# Revit family: Sink-Under_Mount-Lavatory-KOHLER-Bachata-K-2609_1
name_source: partatom
category: Plumbing Fixtures
units: mm (PartAtom-declared; Revit-internal decimal feet)

## family parameters
Cut with Voids When Loaded = No
Host = Face
OmniClass Number = 23.45.05.14.14
OmniClass Title = Sinks/Lavatories
Part Type = Normal
Room Calculation Point = No
Round Connector Dimension = Use Diameter
Shared = No

## types (4) — shared parameters
ADA Compliant = Yes
Assembly Code = D2010400
CW Connection = No
Cold Water Inlet = Cold Water Inlet
Date Modified = 11/24/2024
Default Elevation = 34"
Description = 20 Inch Oval Drop-In/Undermount Bathroom Sink
Drain Included = No
HW Connection = No
Height = 7 3/8"
Hot Water Inlet = Hot Water Inlet
Length = 19 7/8"
Manufacturer = Kohler Co.
MasterFormat 2014 = 22 41 16
MasterFormat 2014 Name = Residential Lavatories and Sinks
Material = 20 Gauge Stainless Steel
Product Documentation Link = https://www.us.kohler.com
Product Name = Bachata
Product Page URL = http://www.us.kohler.com
URL = https://www.us.kohler.com
Vent Connection = No
Waste Connection = Yes
Waste Water Outlet = Waste Water Outlet
Width = 16 11/16"

## per-type parameters (varying)
| type | Finish | Model | Type |
| Satin Finish, Luster Finish | Kohler-Metal-SU-Stainless_Steel_Luster_Finish | K-2609-SU-NA | 1 |
| MU-Mirror Finish | Kohler-Metal-MU-Stainless_Steel_Mirror_Finish | K-2609-MU-NA | 2 |
| Satin Finish, 2MB-Vibrant Brushed Moderne Brass | Kohler-Metal-2MB-Vibrant_Brushed_Moderne_Brass | K-2609-SU-2MB | 3 |
| Satin Finish, BV-Brushed Bronze | Kohler-Metal-BV-Brushed_Bronze | K-2609-SU-BV | 4 |

## geometry (parser evidence)
native form markers: Sweep x4
no freeform markers — native parametric forms only
